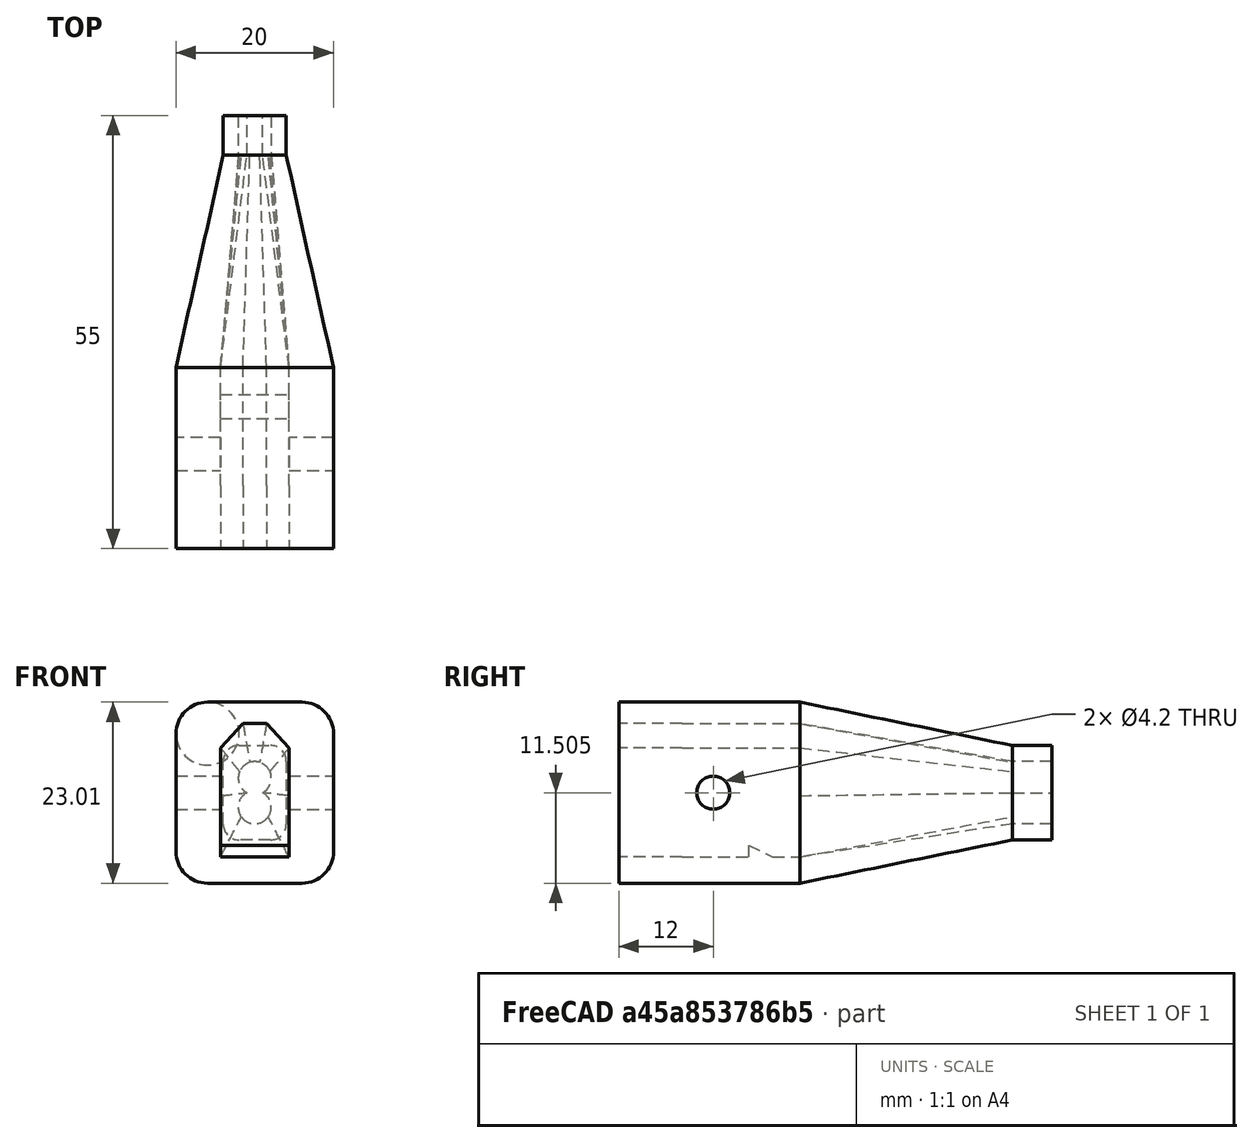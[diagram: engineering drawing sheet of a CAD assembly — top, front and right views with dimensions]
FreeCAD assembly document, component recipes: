
FREECAD ASSEMBLY — COMPONENT RECIPES ("xt60covert008")

This assembly document has 4 components, labeled P0..P3 below (a component is one placed body or linked part). 4 of them carry a construction recipe — the FreeCAD feature program that regenerates the part from scratch, quoted from this document or its linked companion documents; the rest are supplied as boundary geometry only. No exploded tour is included for this assembly.
COMPONENT P0 — recipe-attached ("Body001", modeled in this document).
Construction recipe (the document's own serialized feature program — sketch geometry with constraints, then the solid features built on it; lengths are millimeters unless a unit is written):

FEATURE [Sketcher::SketchObject] Sketch002  label="profileDeBaseSk"
  AttachmentOffset = pos=(0,0,-15) rot=(0,0,1;0rad)
  FullyConstrained = true
  MapMode = 5
  Placement = pos=(0,15,3.3e-15) rot=(1,0,0;1.5708rad)
  Support = -> [XZ_Plane019]
  expr: Constraints[15] = <<coverSp>>.coinRayon
  expr: Constraints[16] = <<coverSp>>.base
  expr: Constraints[17] = <<coverSp>>.haut
  expr: Constraints[18] = <<coverSp>>.baseDistVert
  sketch-geometry (8):
    g0: LineSegment StartX=-6 StartY=19.675 StartZ=0 EndX=6 EndY=19.675 EndZ=0
    g1: LineSegment StartX=10 StartY=15.675 StartZ=0 EndX=10 EndY=0.675 EndZ=0
    g2: LineSegment StartX=6 StartY=-3.325 StartZ=0 EndX=-6 EndY=-3.325 EndZ=0
    g3: LineSegment StartX=-10 StartY=0.675 StartZ=0 EndX=-10 EndY=15.675 EndZ=0
    g4: ArcOfCircle CenterX=-6 CenterY=15.675 CenterZ=0 NormalX=0 NormalY=0 NormalZ=1 AngleXU=0 Radius=4 StartAngle=1.5708 EndAngle=3.14159
    g5: ArcOfCircle CenterX=6 CenterY=15.675 CenterZ=0 NormalX=0 NormalY=0 NormalZ=1 AngleXU=0 Radius=4 StartAngle=-2.7e-15 EndAngle=1.5708
    g6: ArcOfCircle CenterX=6 CenterY=0.675 CenterZ=0 NormalX=0 NormalY=0 NormalZ=1 AngleXU=0 Radius=4 StartAngle=4.71239 EndAngle=6.28319
    g7: ArcOfCircle CenterX=-6 CenterY=0.675 CenterZ=0 NormalX=0 NormalY=0 NormalZ=1 AngleXU=0 Radius=4 StartAngle=3.14159 EndAngle=4.71239
  constraints (19):
    c: Horizontal(g2)
    c: Vertical(g1)
    c: Vertical(g3)
    c: Tangent(g0,g4) = 1.5708
    c: Tangent(g3,g4) = 1.5708
    c: Tangent(g0,g5) = 1.5708
    c: Tangent(g1,g5) = 1.5708
    c: Tangent(g1,g6) = 1.5708
    c: Tangent(g2,g6) = 1.5708
    c: Tangent(g2,g7) = 1.5708
    c: Tangent(g3,g7) = 1.5708
    c: Equal(g6,g5)
    c: Equal(g5,g4)
    c: Equal(g4,g7)
    c: Symmetric(g0,g0,g-2)
    c: Radius(g5) = 4
    c: DistanceX(g3,g1) = 20
    c: DistanceY(g2,g0) = 23
    c: DistanceY(g2,g-1) = 3.325
FEATURE [Sketcher::SketchObject] Sketch003  label="profileExtremiteSk"
  AttachmentOffset = pos=(0,0,-42) rot=(0,0,1;0rad)
  FullyConstrained = true
  MapMode = 5
  Placement = pos=(0,42,9.3e-15) rot=(1,0,0;1.5708rad)
  Support = -> [XZ_Plane019]
  expr: Constraints[14] = <<coverSp>>.extremiteRayon
  expr: Constraints[15] = <<coverSp>>.extremiteLarg
  expr: Constraints[16] = <<coverSp>>.extremiteHaut
  expr: Constraints[21] = <<coverSp>>.centreY
  sketch-geometry (10):
    g0: LineSegment StartX=-2 StartY=14.175 StartZ=0 EndX=2 EndY=14.175 EndZ=0
    g1: LineSegment StartX=4 StartY=12.175 StartZ=0 EndX=4 EndY=4.175 EndZ=0
    g2: LineSegment StartX=2 StartY=2.175 StartZ=0 EndX=-2 EndY=2.175 EndZ=0
    g3: LineSegment StartX=-4 StartY=4.175 StartZ=0 EndX=-4 EndY=12.175 EndZ=0
    g4: ArcOfCircle CenterX=-2 CenterY=12.175 CenterZ=0 NormalX=0 NormalY=0 NormalZ=1 AngleXU=0 Radius=2 StartAngle=1.5708 EndAngle=3.14159
    g5: ArcOfCircle CenterX=2 CenterY=12.175 CenterZ=0 NormalX=0 NormalY=0 NormalZ=1 AngleXU=0 Radius=2 StartAngle=0 EndAngle=1.5708
    g6: ArcOfCircle CenterX=2 CenterY=4.175 CenterZ=0 NormalX=0 NormalY=0 NormalZ=1 AngleXU=0 Radius=2 StartAngle=4.71239 EndAngle=6.28319
    g7: ArcOfCircle CenterX=-2 CenterY=4.175 CenterZ=0 NormalX=0 NormalY=0 NormalZ=1 AngleXU=0 Radius=2 StartAngle=3.14159 EndAngle=4.71239
    g8: LineSegment StartX=-2 StartY=12.175 StartZ=0 EndX=-2 EndY=4.175 EndZ=0
    g9: GeomPoint X=-2 Y=8.175 Z=0
  constraints (22):
    c: Horizontal(g0)
    c: Vertical(g1)
    c: Vertical(g3)
    c: Tangent(g0,g4) = 1.5708
    c: Tangent(g3,g4) = 1.5708
    c: Tangent(g0,g5) = 1.5708
    c: Tangent(g1,g5) = 1.5708
    c: Tangent(g1,g6) = 1.5708
    c: Tangent(g2,g6) = 1.5708
    c: Tangent(g2,g7) = 1.5708
    c: Tangent(g3,g7) = 1.5708
    c: Equal(g4,g5)
    c: Equal(g5,g6)
    c: Equal(g6,g7)
    c: Radius(g5) = 2
    c: DistanceX(g3,g1) = 8
    c: DistanceY(g2,g0) = 12
    c: Symmetric(g2,g2,g-2)
    c: Coincident(g8,g4)
    c: Coincident(g8,g7)
    c: Symmetric(g7,g4,g9)
    c: DistanceY(g-1,g9) = 8.175
FEATURE [PartDesign::AdditiveLoft] AdditiveLoft  label="manchonPlein"
  Closed = false
  Placement = pos=(0,0,0) rot=(1,0,0;1.5708rad)
  Profile = -> Sketch002
  Ruled = false
  Sections = -> [Sketch003]
FEATURE [PartDesign::Body] Body001
  Group = -> [Sketch002,Sketch003,AdditiveLoft]
  Origin = -> Origin023
  Tip = -> AdditiveLoft
COMPONENT P1 — recipe-attached ("xtInsertVisLnk", a linked part whose construction recipe lives in a companion FreeCAD document of the same project; that document's serialized recipe follows).
Construction recipe (the companion document, serialized — sketch geometry with constraints, then the solid features built on it; lengths are millimeters unless a unit is written):

FCSTD DOCUMENT  (FreeCAD 0.20R29177 (Git))
Label: xt60_insert_vis
License: All rights reserved
LicenseURL: http://en.wikipedia.org/wiki/All_rights_reserved
objects: App::Part×3, Sketcher::SketchObject×2, PartDesign::Chamfer×2, Part::Feature×1, PartDesign::Pad×1, PartDesign::Pocket×1, PartDesign::Body×1, App::Link×1
note: 12 computed .brp shape members not serialized (recipe doc carries the construction recipe); baked Part::Feature solids carry a one-line shape summary decoded from their .brp
EXTERNAL_REF file=../elementsCommun/xt_001.FCStd obj=Part

FEATURE [Part::Feature] Solid002  label="RUTHEX_M3x5_7"
  Placement = pos=(-11.5,0,-0.2) rot=(0,0,1;0rad)
  shape: bbox 4.583 x 5.705 x 4.583 mm, 200 faces (baked)
FEATURE [App::Part] Part003  label="ZSB_RUTHEX_M3_5.7_001"
  Group = -> [Solid002]
  Origin = -> Origin006
  Placement = pos=(-15.5,-3.9,18.8) rot=(0,0,1;3.14159rad)
FEATURE [Sketcher::SketchObject] Sketch025
  FullyConstrained = false
  MapMode = 5
  Support = -> [XY_Plane008]
  sketch-geometry (1):
    g0: Circle CenterX=0 CenterY=0 CenterZ=0 NormalX=0 NormalY=0 NormalZ=1 AngleXU=0 Radius=1.5
  constraints (2):
    c: Coincident(g0,g-1)
    c: Diameter(g0) = 3
FEATURE [Sketcher::SketchObject] Sketch026
  FullyConstrained = false
  MapMode = 5
  Support = -> [XY_Plane008]
  sketch-geometry (7):
    g0: LineSegment StartX=0.433013 StartY=-0.75 StartZ=0 EndX=0.866025 EndY=1.25568e-11 EndZ=0
    g1: LineSegment StartX=0.866025 StartY=1.25568e-11 StartZ=0 EndX=0.433013 EndY=0.75 EndZ=0
    g2: LineSegment StartX=0.433013 StartY=0.75 StartZ=0 EndX=-0.433013 EndY=0.75 EndZ=0
    g3: LineSegment StartX=-0.433013 StartY=0.75 StartZ=0 EndX=-0.866025 EndY=2.91366e-11 EndZ=0
    g4: LineSegment StartX=-0.866025 StartY=2.91366e-11 StartZ=0 EndX=-0.433013 EndY=-0.75 EndZ=0
    g5: LineSegment StartX=-0.433013 StartY=-0.75 StartZ=0 EndX=0.433013 EndY=-0.75 EndZ=0
    g6: Circle CenterX=0 CenterY=0 CenterZ=0 NormalX=0 NormalY=0 NormalZ=1 AngleXU=0 Radius=0.866025
  constraints (16):
    c: Coincident(g0,g1)
    c: Coincident(g1,g2)
    c: Coincident(g2,g3)
    c: Coincident(g3,g4)
    c: Coincident(g4,g5)
    c: Coincident(g5,g0)
    c: Equal(g0, g1-g5) x5
    c: PointOnObject(g0,g6)
    c: PointOnObject(g1,g6)
    c: PointOnObject(g2,g6)
    c: PointOnObject(g3,g6)
    c: PointOnObject(g4,g6)
    c: PointOnObject(g5,g6)
    c: Coincident(g6,g-1)
    c: Horizontal(g2)
    c: DistanceY(g0,g1) = 1.5
FEATURE [PartDesign::Pad] Pad012
  AllowMultiFace = false
  Direction = (1,1,1)
  Length = 6
  Length2 = 100
  Profile = -> Sketch025
  Type = 0
FEATURE [PartDesign::Chamfer] Chamfer
  Angle = 45
  Base = -> Pad012 [Edge3]
  BaseFeature = -> Pad012
  ChamferType = 0
  FlipDirection = false
  Size = 1.4
  Size2 = 1
  SupportTransform = false
  UseAllEdges = false
FEATURE [PartDesign::Pocket] Pocket013
  AllowMultiFace = false
  BaseFeature = -> Chamfer
  Direction = (1,1,1)
  Length = 1.5
  Length2 = 100
  Profile = -> Sketch026
  Reversed = true
  Type = 0
FEATURE [PartDesign::Chamfer] Chamfer001
  Angle = 45
  Base = -> Pocket013 [Edge3]
  BaseFeature = -> Pocket013
  ChamferType = 0
  FlipDirection = false
  Size = 0.1
  Size2 = 1
  SupportTransform = false
  UseAllEdges = false
FEATURE [PartDesign::Body] Body005  label="bodyVisPointeauM3x10_001"
  Group = -> [Sketch025,Pad012,Chamfer,Sketch026,Pocket013,Chamfer001]
  Origin = -> Origin013
  Tip = -> Chamfer001
FEATURE [App::Part] Part007  label="partVisPointeauM3x10_001"
  Group = -> [Body005]
  Origin = -> Origin012
  Placement = pos=(-4,-4.4,18.6) rot=(1,0,0;1.5708rad)
FEATURE [App::Link] Link  label="xt60Male001"
  LinkPlacement = pos=(-7.60001,-13.95,10.25) rot=(0,0,1;1.5708rad)
  LinkedObject = -> <external ../elementsCommun/xt_001.FCStd>#Part
  Placement = pos=(-7.60001,-13.95,10.25) rot=(0,0,1;1.5708rad)
FEATURE [App::Part] Part010  label="xtVisInsertFix"
  Group = -> [Part003,Part007,Link]
  Origin = -> Origin021
  Placement = pos=(0,13.942,-10.258) rot=(0,0,1;0rad)
COMPONENT P2 — recipe-attached ("xt60FemLnk", a linked part whose construction recipe lives in a companion FreeCAD document of the same project; that document's serialized recipe follows).
Construction recipe (the companion document, serialized — sketch geometry with constraints, then the solid features built on it; lengths are millimeters unless a unit is written):

FCSTD DOCUMENT  (FreeCAD 0.20R29177 (Git))
Label: xt60Fem
License: All rights reserved
LicenseURL: http://en.wikipedia.org/wiki/All_rights_reserved
objects: App::Part×4, Part::Feature×2, Sketcher::SketchObject×2, PartDesign::Chamfer×2, PartDesign::Pad×1, PartDesign::Pocket×1, PartDesign::Body×1
note: 13 computed .brp shape members not serialized (recipe doc carries the construction recipe); baked Part::Feature solids carry a one-line shape summary decoded from their .brp

FEATURE [Part::Feature] Part__Feature  label="XT60FemaleConnector"
  shape: bbox 20.5 x 7.501 x 16.55 mm, 417 faces, 3 solids (baked)
FEATURE [App::Part] Part001  label="xt60fem"
  Group = -> [Part__Feature]
  Origin = -> Origin004
  Placement = pos=(-26.5,-14,16.7) rot=(1,0,0;3.14159rad)
FEATURE [Part::Feature] Solid003  label="RUTHEX_M3x5_008"
  Placement = pos=(-11,0,0) rot=(0,0,1;0rad)
  shape: bbox 4.583 x 5.705 x 4.583 mm, 200 faces (baked)
FEATURE [App::Part] Part004  label="ZSB_RUTHEX_M3_5.7_002"
  Group = -> [Solid003]
  Origin = -> Origin007
  Placement = pos=(-34,3.7e-15,16.6) rot=(0,0,1;3.14159rad)
FEATURE [Sketcher::SketchObject] Sketch027
  FullyConstrained = false
  MapMode = 5
  Support = -> [XY_Plane010]
  sketch-geometry (7):
    g0: LineSegment StartX=0.433013 StartY=-0.75 StartZ=0 EndX=0.866025 EndY=1.25568e-11 EndZ=0
    g1: LineSegment StartX=0.866025 StartY=1.25568e-11 StartZ=0 EndX=0.433013 EndY=0.75 EndZ=0
    g2: LineSegment StartX=0.433013 StartY=0.75 StartZ=0 EndX=-0.433013 EndY=0.75 EndZ=0
    g3: LineSegment StartX=-0.433013 StartY=0.75 StartZ=0 EndX=-0.866025 EndY=2.91366e-11 EndZ=0
    g4: LineSegment StartX=-0.866025 StartY=2.91366e-11 StartZ=0 EndX=-0.433013 EndY=-0.75 EndZ=0
    g5: LineSegment StartX=-0.433013 StartY=-0.75 StartZ=0 EndX=0.433013 EndY=-0.75 EndZ=0
    g6: Circle CenterX=0 CenterY=0 CenterZ=0 NormalX=0 NormalY=0 NormalZ=1 AngleXU=0 Radius=0.866025
  constraints (16):
    c: Coincident(g0,g1)
    c: Coincident(g1,g2)
    c: Coincident(g2,g3)
    c: Coincident(g3,g4)
    c: Coincident(g4,g5)
    c: Coincident(g5,g0)
    c: Equal(g0, g1-g5) x5
    c: PointOnObject(g0,g6)
    c: PointOnObject(g1,g6)
    c: PointOnObject(g2,g6)
    c: PointOnObject(g3,g6)
    c: PointOnObject(g4,g6)
    c: PointOnObject(g5,g6)
    c: Coincident(g6,g-1)
    c: Horizontal(g2)
    c: DistanceY(g0,g1) = 1.5
FEATURE [Sketcher::SketchObject] Sketch028
  FullyConstrained = false
  MapMode = 5
  Support = -> [XY_Plane010]
  sketch-geometry (1):
    g0: Circle CenterX=0 CenterY=0 CenterZ=0 NormalX=0 NormalY=0 NormalZ=1 AngleXU=0 Radius=1.5
  constraints (2):
    c: Coincident(g0,g-1)
    c: Diameter(g0) = 3
FEATURE [PartDesign::Pad] Pad013
  AllowMultiFace = false
  Direction = (1,1,1)
  Length = 10
  Length2 = 100
  Profile = -> Sketch028
  Type = 0
FEATURE [PartDesign::Chamfer] Chamfer003
  Angle = 45
  Base = -> Pad013 [Edge3]
  BaseFeature = -> Pad013
  ChamferType = 0
  FlipDirection = false
  Size = 1.4
  Size2 = 1
  SupportTransform = false
  UseAllEdges = false
FEATURE [PartDesign::Pocket] Pocket014
  AllowMultiFace = false
  BaseFeature = -> Chamfer003
  Direction = (1,1,1)
  Length = 1.5
  Length2 = 100
  Profile = -> Sketch027
  Reversed = true
  Type = 0
FEATURE [PartDesign::Chamfer] Chamfer002
  Angle = 45
  Base = -> Pocket014 [Edge3]
  BaseFeature = -> Pocket014
  ChamferType = 0
  FlipDirection = false
  Size = 0.1
  Size2 = 1
  SupportTransform = false
  UseAllEdges = false
FEATURE [PartDesign::Body] Body006  label="bodyVisPointeauM3x10_002"
  Group = -> [Sketch028,Pad013,Chamfer003,Sketch027,Pocket014,Chamfer002]
  Origin = -> Origin015
  Tip = -> Chamfer002
FEATURE [App::Part] Part008  label="partVisPointeauM3x10_002"
  Group = -> [Body006]
  Origin = -> Origin014
  Placement = pos=(-23.1,-0.5,16.6) rot=(1,0,0;1.5708rad)
FEATURE [App::Part] Part011  label="xtVisInertMob"
  Group = -> [Part001,Part004,Part008]
  Origin = -> Origin022
COMPONENT P3 — recipe-attached ("covert", modeled in this document).
Construction recipe (the document's own serialized feature program — sketch geometry with constraints, then the solid features built on it; lengths are millimeters unless a unit is written):

FEATURE [Sketcher::SketchObject] Sketch  label="formBaseSk"
  FullyConstrained = true
  MapMode = 5
  Placement = pos=(0,0,0) rot=(1,0,0;1.5708rad)
  Support = -> [XZ_Plane018]
  expr: Constraints[14] = <<coverSp>>.base
  expr: Constraints[15] = <<coverSp>>.coinRayon
  expr: Constraints[16] = <<coverSp>>.haut
  expr: Constraints[29] = <<paramSp>>.xtHaut
  expr: Constraints[30] = <<paramSp>>.xtBase
  expr: Constraints[31] = <<coverSp>>.xtToitHaut
  expr: Constraints[32] = xt_001#<<xtSp>>.fetierLarg
  expr: Constraints[33] = <<coverSp>>.baseDistVert
  sketch-geometry (18):
    g0: LineSegment StartX=-6 StartY=19.675 StartZ=0 EndX=6 EndY=19.675 EndZ=0
    g1: LineSegment StartX=10 StartY=15.675 StartZ=0 EndX=10 EndY=0.675 EndZ=0
    g2: LineSegment StartX=6 StartY=-3.325 StartZ=0 EndX=-6 EndY=-3.325 EndZ=0
    g3: LineSegment StartX=-10 StartY=0.675 StartZ=0 EndX=-10 EndY=15.675 EndZ=0
    g4: ArcOfCircle CenterX=-6 CenterY=15.675 CenterZ=0 NormalX=0 NormalY=0 NormalZ=1 AngleXU=0 Radius=4 StartAngle=1.5708 EndAngle=3.14159
    g5: ArcOfCircle CenterX=6 CenterY=15.675 CenterZ=0 NormalX=0 NormalY=0 NormalZ=1 AngleXU=0 Radius=4 StartAngle=0 EndAngle=1.5708
    g6: ArcOfCircle CenterX=-6 CenterY=0.675 CenterZ=0 NormalX=0 NormalY=0 NormalZ=1 AngleXU=0 Radius=4 StartAngle=3.14159 EndAngle=4.71239
    g7: ArcOfCircle CenterX=6 CenterY=0.675 CenterZ=0 NormalX=0 NormalY=0 NormalZ=1 AngleXU=0 Radius=4 StartAngle=4.71239 EndAngle=6.28319
    g8: LineSegment StartX=-4.35 StartY=0 StartZ=0 EndX=4.35 EndY=0 EndZ=0
    g9: LineSegment StartX=4.35 StartY=0 StartZ=0 EndX=4.35 EndY=13.85 EndZ=0
    g10: LineSegment StartX=4.35 StartY=13.85 StartZ=0 EndX=1.5 EndY=16.95 EndZ=0
    g11: LineSegment StartX=1.5 StartY=16.95 StartZ=0 EndX=-1.5 EndY=16.95 EndZ=0
    g12: LineSegment StartX=-1.5 StartY=16.95 StartZ=0 EndX=-4.35 EndY=13.85 EndZ=0
    g13: LineSegment StartX=-4.35 StartY=13.85 StartZ=0 EndX=-4.35 EndY=0 EndZ=0
    g14: LineSegment StartX=-6 StartY=15.675 StartZ=0 EndX=-6 EndY=0.675 EndZ=0
    g15: GeomPoint X=-6 Y=8.175 Z=0
    g16: LineSegment StartX=0 StartY=16.95 StartZ=0 EndX=0 EndY=0 EndZ=0
    g17: GeomPoint X=0 Y=8.475 Z=0
  constraints (43):
    c: Horizontal(g2)
    c: Vertical(g1)
    c: Tangent(g0,g4) = 1.5708
    c: Tangent(g3,g4) = 1.5708
    c: Tangent(g0,g5) = 1.5708
    c: Tangent(g1,g5) = 1.5708
    c: Tangent(g2,g6) = 1.5708
    c: Tangent(g3,g6) = 1.5708
    c: Tangent(g1,g7) = 1.5708
    c: Tangent(g2,g7) = 1.5708
    c: Symmetric(g0,g0,g-2)
    c: Symmetric(g1,g3,g-2)
    c: Equal(g7,g6)
    c: Equal(g5,g7)
    c: DistanceX(g3,g1) = 20
    c: Radius(g5) = 4
    c: DistanceY(g2,g0) = 23
    c: PointOnObject(g8,g-1)
    c: Horizontal(g8)
    c: Coincident(g8,g9)
    c: Vertical(g9)
    c: Coincident(g9,g10)
    c: Coincident(g10,g11)
    c: Coincident(g11,g12)
    c: Coincident(g12,g13)
    c: Coincident(g13,g8)
    c: Vertical(g13)
    c: Symmetric(g11,g10,g-2)
    c: Symmetric(g12,g9,g-2)
    c: DistanceY(g8,g9) = 13.85
    c: DistanceX(g8,g8) = 8.7
    c: DistanceY(g9,g10) = 3.1
    c: DistanceX(g11,g10) = 3
    c: DistanceY(g2,g-1) = 3.325
    c: Coincident(g14,g4)
    c: Coincident(g14,g6)
    c: Symmetric(g6,g4,g15)
    c: DistanceY(g-1,g15) = 8.175
    c: PointOnObject(g16,g11)
    c: Coincident(g16,g-1)
    c: Vertical(g16)
    c: Symmetric(g16,g16,g17)
    c: DistanceY(g16,g17) = 8.475
FEATURE [PartDesign::Pad] Pad  label="formeDeBase"
  Direction = (0,-1,-2e-16)
  Length = 15
  Length2 = 100
  Placement = pos=(0,0,0) rot=(1,0,0;1.5708rad)
  Profile = -> Sketch
  Reversed = true
  Type = 0
FEATURE [PartDesign::Boolean] Boolean  label="corpsAvecManchonPlein"
  BaseFeature = -> Pad
  Group = -> [Body001]
  Type = 0
FEATURE [Sketcher::SketchObject] Sketch005
  ExternalGeometry = -> [Boolean]
  FullyConstrained = true
  MapMode = 5
  Placement = pos=(0,42,9.2e-15) rot=(0,0.707107,0.707107;3.14159rad)
  Support = -> [Boolean]
  expr: Constraints[18] = <<coverSp>>.trousFilsDiam
  expr: Constraints[24] = <<coverSp>>.trousFilsEntraxe
  expr: Constraints[25] = <<coverSp>>.trouFilPosY
  sketch-geometry (12):
    g0: LineSegment StartX=-2 StartY=14.175 StartZ=0 EndX=2 EndY=14.175 EndZ=0
    g1: LineSegment StartX=4 StartY=12.175 StartZ=0 EndX=4 EndY=4.175 EndZ=0
    g2: LineSegment StartX=2 StartY=2.175 StartZ=0 EndX=-2 EndY=2.175 EndZ=0
    g3: LineSegment StartX=-4 StartY=4.175 StartZ=0 EndX=-4 EndY=12.175 EndZ=0
    g4: ArcOfCircle CenterX=-2 CenterY=12.175 CenterZ=0 NormalX=0 NormalY=0 NormalZ=1 AngleXU=0 Radius=2 StartAngle=1.5708 EndAngle=3.14159
    g5: ArcOfCircle CenterX=2 CenterY=12.175 CenterZ=0 NormalX=0 NormalY=0 NormalZ=1 AngleXU=0 Radius=2 StartAngle=0 EndAngle=1.5708
    g6: ArcOfCircle CenterX=2 CenterY=4.175 CenterZ=0 NormalX=0 NormalY=0 NormalZ=1 AngleXU=0 Radius=2 StartAngle=4.71239 EndAngle=6.28319
    g7: ArcOfCircle CenterX=-2 CenterY=4.175 CenterZ=0 NormalX=0 NormalY=0 NormalZ=1 AngleXU=0 Radius=2 StartAngle=3.14159 EndAngle=4.71239
    g8: ArcOfCircle CenterX=0 CenterY=10.025 CenterZ=0 NormalX=0 NormalY=0 NormalZ=1 AngleXU=0 Radius=2.1 StartAngle=5.20531 EndAngle=10.5026
    g9: ArcOfCircle CenterX=0 CenterY=6.325 CenterZ=0 NormalX=0 NormalY=0 NormalZ=1 AngleXU=0 Radius=2.1 StartAngle=2.06372 EndAngle=7.36106
    g10: LineSegment StartX=0 StartY=6.325 StartZ=0 EndX=0 EndY=10.025 EndZ=0
    g11: GeomPoint X=0 Y=8.175 Z=0
  constraints (26):
    c: Horizontal(g0)
    c: Vertical(g3)
    c: Tangent(g0,g4) = 1.5708
    c: Tangent(g3,g4) = 1.5708
    c: Tangent(g0,g5) = 1.5708
    c: Tangent(g1,g5) = 1.5708
    c: Tangent(g1,g6) = 1.5708
    c: Tangent(g2,g6) = 1.5708
    c: Tangent(g2,g7) = 1.5708
    c: Tangent(g3,g7) = 1.5708
    c: Coincident(g0,g-4)
    c: Coincident(g3,g-10)
    c: Coincident(g1,g-7)
    c: Coincident(g2,g-8)
    c: Coincident(g1,g-6)
    c: PointOnObject(g8,g-2)
    c: PointOnObject(g9,g-2)
    c: Equal(g8,g9)
    c: Diameter(g8) = 4.2
    c: Coincident(g8,g9)
    c: Coincident(g8,g9)
    c: Coincident(g10,g9)
    c: Coincident(g10,g8)
    c: Symmetric(g9,g8,g11)
    c: DistanceY(g9,g8) = 3.7
    c: DistanceY(g-1,g11) = 8.175
FEATURE [Sketcher::SketchObject] Sketch006
  ExternalGeometry = -> [Boolean]
  FullyConstrained = true
  MapMode = 5
  Placement = pos=(0,15,6e-15) rot=(1,0,0;1.5708rad)
  Support = -> [Boolean]
  sketch-geometry (6):
    g0: LineSegment StartX=-1.5 StartY=16.95 StartZ=0 EndX=-4.35 EndY=13.85 EndZ=0
    g1: LineSegment StartX=-4.35 StartY=13.85 StartZ=0 EndX=-4.35 EndY=0 EndZ=0
    g2: LineSegment StartX=-4.35 StartY=0 StartZ=0 EndX=4.35 EndY=0 EndZ=0
    g3: LineSegment StartX=4.35 StartY=0 StartZ=0 EndX=4.35 EndY=13.85 EndZ=0
    g4: LineSegment StartX=4.35 StartY=13.85 StartZ=0 EndX=1.5 EndY=16.95 EndZ=0
    g5: LineSegment StartX=1.5 StartY=16.95 StartZ=0 EndX=-1.5 EndY=16.95 EndZ=0
  constraints (13):
    c: Coincident(g0,g1)
    c: Vertical(g1)
    c: Coincident(g1,g2)
    c: Horizontal(g2)
    c: Coincident(g2,g3)
    c: Coincident(g3,g4)
    c: Coincident(g4,g5)
    c: Coincident(g5,g0)
    c: Coincident(g0,g-8)
    c: Coincident(g0,g-4)
    c: Coincident(g4,g-5)
    c: Coincident(g3,g-6)
    c: Coincident(g2,g-7)
FEATURE [PartDesign::SubtractiveLoft] SubtractiveLoft
  BaseFeature = -> Boolean
  Closed = false
  Profile = -> Sketch006
  Ruled = false
  Sections = -> [Sketch005]
FEATURE [PartDesign::Pad] Pad001  label="extremite"
  BaseFeature = -> SubtractiveLoft
  Direction = (0,1,2e-16)
  Length = 5
  Length2 = 10
  Profile = -> SubtractiveLoft [Face19]
  Type = 0
FEATURE [Sketcher::SketchObject] Sketch007
  FullyConstrained = true
  MapMode = 5
  Placement = pos=(0,0,0) rot=(0.57735,0.57735,0.57735;2.0944rad)
  Support = -> [YZ_Plane018]
  expr: Constraints[0] = <<coverSp>>.xtTrouDiam
  expr: Constraints[1] = <<coverSp>>.xtTrouPosX
  expr: Constraints[2] = Spreadsheet.xtTrouPosY
  sketch-geometry (1):
    g0: Circle CenterX=4 CenterY=8.175 CenterZ=0 NormalX=0 NormalY=0 NormalZ=1 AngleXU=0 Radius=2.1
  constraints (3):
    c: Diameter(g0) = 4.2
    c: DistanceX(g-1,g0) = 4
    c: DistanceY(g-1,g0) = 8.175
FEATURE [PartDesign::Pocket] Pocket  label="trouInsert"
  BaseFeature = -> Pad001
  Direction = (-1,2e-16,-3e-16)
  Length = 20
  Length2 = 5
  Midplane = true
  Profile = -> Sketch007
  ReferenceAxis = -> Sketch007 [N_Axis]
  Type = 0
  expr: Length = <<coverSp>>.base
FEATURE [Sketcher::SketchObject] Sketch008
  ExternalGeometry = -> [Sketch]
  FullyConstrained = true
  MapMode = 5
  Placement = pos=(0,0,0) rot=(1,0,0;1.5708rad)
  Support = -> [XZ_Plane018]
  sketch-geometry (14):
    g0: ArcOfCircle CenterX=-6 CenterY=15.675 CenterZ=0 NormalX=0 NormalY=0 NormalZ=1 AngleXU=0 Radius=4 StartAngle=1.5708 EndAngle=3.14159
    g1: ArcOfCircle CenterX=6 CenterY=0.675 CenterZ=0 NormalX=0 NormalY=0 NormalZ=1 AngleXU=0 Radius=4 StartAngle=4.71239 EndAngle=6.28319
    g2: ArcOfCircle CenterX=6 CenterY=15.675 CenterZ=0 NormalX=0 NormalY=0 NormalZ=1 AngleXU=0 Radius=4 StartAngle=0 EndAngle=1.5708
    g3: ArcOfCircle CenterX=-6 CenterY=0.675 CenterZ=0 NormalX=0 NormalY=0 NormalZ=1 AngleXU=0 Radius=4 StartAngle=3.14159 EndAngle=4.71239
    g4: LineSegment StartX=-10 StartY=15.675 StartZ=0 EndX=-10 EndY=0.675 EndZ=0
    g5: LineSegment StartX=-6.00002 StartY=19.675 StartZ=0 EndX=6 EndY=19.675 EndZ=0
    g6: LineSegment StartX=10 StartY=15.675 StartZ=0 EndX=10 EndY=0.675 EndZ=0
    g7: LineSegment StartX=-6 StartY=-3.325 StartZ=0 EndX=6 EndY=-3.325 EndZ=0
    g8: LineSegment StartX=-4.35 StartY=0 StartZ=0 EndX=-4.35 EndY=13.85 EndZ=0
    g9: LineSegment StartX=-4.35 StartY=13.85 StartZ=0 EndX=-1.5 EndY=16.95 EndZ=0
    g10: LineSegment StartX=-1.5 StartY=16.95 StartZ=0 EndX=1.5 EndY=16.95 EndZ=0
    g11: LineSegment StartX=1.5 StartY=16.95 StartZ=0 EndX=4.35 EndY=13.85 EndZ=0
    g12: LineSegment StartX=4.35 StartY=13.85 StartZ=0 EndX=4.35 EndY=0 EndZ=0
    g13: LineSegment StartX=4.35 StartY=0 StartZ=0 EndX=-4.35 EndY=0 EndZ=0
  constraints (30):
    c: Coincident(g0,g-3)
    c: Coincident(g0,g-3)
    c: Coincident(g1,g-4)
    c: Coincident(g1,g-4)
    c: Coincident(g3,g-6)
    c: Coincident(g3,g-6)
    c: Coincident(g4,g0)
    c: Coincident(g4,g3)
    c: Vertical(g4)
    c: Coincident(g5,g0)
    c: Coincident(g7,g3)
    c: Coincident(g7,g1)
    c: Vertical(g6)
    c: Horizontal(g5)
    c: Tangent(g6,g1) = 1.5708
    c: Coincident(g2,g-5)
    c: Tangent(g6,g2) = 1.5708
    c: Tangent(g5,g2) = 1.5708
    c: Coincident(g-7,g8)
    c: Coincident(g8,g-8)
    c: Coincident(g8,g9)
    c: Coincident(g9,g-9)
    c: Coincident(g9,g10)
    c: Coincident(g10,g-10)
    c: Coincident(g10,g11)
    c: Coincident(g11,g-11)
    c: Coincident(g11,g12)
    c: Coincident(g12,g-11)
    c: Coincident(g12,g13)
    c: Coincident(g13,g8)
FEATURE [PartDesign::Pad] Pad002  label="extensionFem"
  BaseFeature = -> Pocket
  Direction = (0,-1,-2e-16)
  Length = 8
  Length2 = 10
  Profile = -> Sketch008
  ReferenceAxis = -> Sketch008 [N_Axis]
  Type = 0
  expr: Length = <<paramSp>>.extensionFem
FEATURE [Sketcher::SketchObject] Sketch009
  FullyConstrained = true
  MapMode = 5
  Placement = pos=(0,0,0) rot=(0.57735,0.57735,0.57735;2.0944rad)
  Support = -> [YZ_Plane018]
  expr: Constraints[6] = <<paramSp>>.buteeX
  expr: Constraints[7] = <<coverSp>>.buteeEp
  expr: Constraints[8] = <<coverSp>>.buteeH
  sketch-geometry (3):
    g0: LineSegment StartX=8.55 StartY=0 StartZ=0 EndX=8.55 EndY=1.5 EndZ=0
    g1: LineSegment StartX=8.55 StartY=1.5 StartZ=0 EndX=11.55 EndY=0 EndZ=0
    g2: LineSegment StartX=11.55 StartY=0 StartZ=0 EndX=8.55 EndY=0 EndZ=0
  constraints (9):
    c: PointOnObject(g0,g-1)
    c: Vertical(g0)
    c: Coincident(g0,g1)
    c: PointOnObject(g1,g-1)
    c: Coincident(g1,g2)
    c: Coincident(g2,g0)
    c: DistanceX(g-1,g0) = 8.55
    c: DistanceX(g0,g1) = 3
    c: DistanceY(g0,g0) = 1.5
FEATURE [PartDesign::Pad] Pad003  label="butee"
  BaseFeature = -> Pad002
  Direction = (1,-2e-16,3e-16)
  Length = 8.7
  Length2 = 10
  Midplane = true
  Profile = -> Sketch009
  ReferenceAxis = -> Sketch009 [N_Axis]
  Type = 0
  expr: Length = <<paramSp>>.xtBase
FEATURE [PartDesign::Body] Body  label="covertBdy"
  Group = -> [Sketch,Pad,Boolean,Sketch005,Sketch006,SubtractiveLoft,Pad001,Sketch007,Pocket,Sketch008,Pad002,Sketch009,Pad003]
  Origin = -> Origin022
  Tip = -> Pad003
PROVENANCE & LICENSES
A FreeCAD (.FCStd) document from a public repository crawl; recipes are the document's own serialized feature recipes (and, for linked parts, companion documents' recipes).
License: as declared in the source repository (recorded in the dataset sidecar).
